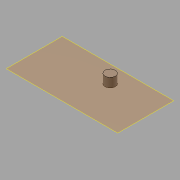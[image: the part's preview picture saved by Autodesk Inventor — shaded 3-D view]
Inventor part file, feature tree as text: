
AUTODESK INVENTOR PART (.ipt)
format: ipt  version: 2015 (Build 190159000, 159)  size: 242,688 bytes
history: native  units: mm
features: sketch x11, extrude x11, reference x7, plane x5
ambient origin geometry x8: Origin, YZ Plane, XZ Plane, XY Plane, X Axis, Y Axis, Z Axis, Center Point
bodies: Body1 (feature_tree)
feature tree (34):
  plane  "Work Plane1"
  sketch  "Sketch1"  dims[d2=10.0mm d3=0.0mm d4=10.0mm d5=0.0mm]
  plane  "Work Plane2"
  plane  "Work Plane3"
  extrude  "Extrusion2"  Depth=10.0mm TaperAngle=0.0deg
  sketch  "Sketch2"  dims[d6=10.0mm d7=0.0mm d8=10.0mm d9=0.0mm]
  plane  "Work Plane4"
  extrude  "Extrusion3"  Depth=10.0mm TaperAngle=0.0deg
  extrude  "Extrusion4"  Depth=1.0mm TaperAngle=0.0deg
  sketch  "Sketch4"  dims[d18=1.0mm d25=8.5mm d26=0.0mm]
  plane  "Work Plane5"
  extrude  "Extrusion5"  Depth=8.5mm TaperAngle=0.0deg
  extrude  "Extrusion6"  Depth=3.0mm
  extrude  "Extrusion7"  Depth=5.0mm TaperAngle=0.0deg
  extrude  "Extrusion9"  Depth=1.0mm
  extrude  "Extrusion12"  Depth=3.0mm
  extrude  "Extrusion13"  Depth=5.0mm TaperAngle=0.0deg
  extrude  "Extrusion14"  [1 undecoded]
  extrude  "Extrusion15"  [1 undecoded]
  reference  "Reference1"
  reference  "Reference2"
  sketch  "Sketch3"  dims[d10=10.0mm d11=0.0mm d16=1.0mm d17=0.0mm]
  reference  "Reference3"
  reference  "Reference4"
  sketch  "Sketch5"  dims[d51=6.0mm d52=0.0mm d53=3.0mm]
  reference  "Reference5"
  sketch  "Sketch6"  dims[d54=1.0mm d55=5.0mm d56=0.0mm]
  sketch  "Sketch7"  dims[d57=3.0mm d58=1.0mm]
  reference  "Reference7"
  reference  "Reference8"
  sketch  "Sketch11"  dims[d59=5.0mm d60=0.0mm d61=3.0mm]
  sketch  "Sketch12"  dims[d62=1.0mm d63=5.0mm d64=0.0mm]
  sketch  "Sketch13"
  sketch  "Sketch14"
note: 2 required parameter values undecoded (feature->parameter linkage not recoverable at this tier; creation-order binding heuristic only, values carry confidence <= 0.55)
